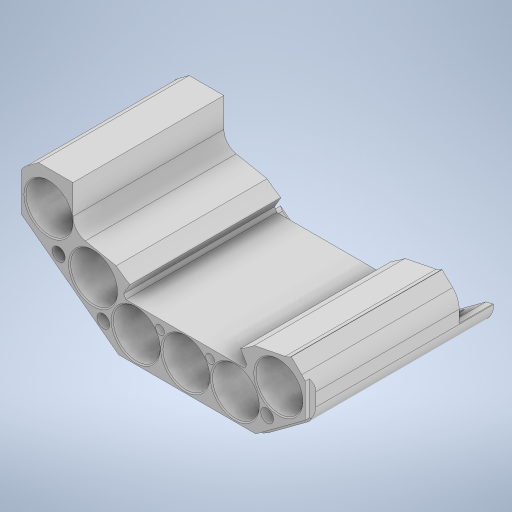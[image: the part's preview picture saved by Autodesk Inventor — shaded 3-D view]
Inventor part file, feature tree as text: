
AUTODESK INVENTOR PART (.ipt)
format: ipt  version: 2023.4 (Build 274418000, 418)  size: 566,272 bytes
history: native  units: mm
features: extrude x11, sketch x11, chamfer x3, projected_geometry x2, thicken_offset x1, fillet x1, mirror x1
ambient origin geometry x8: Origin, YZ Plane, XZ Plane, XY Plane, X Axis, Y Axis, Z Axis, Center Point
bodies: Solid1 (feature_tree)
feature tree (30):
  extrude  "Extrusion1"  Depth=70.0mm
  thicken_offset  "Thicken1"
  extrude  "Extrusion2"  Depth=21.7mm
  extrude  "Extrusion3"  Depth=21.7mm
  chamfer  "Chamfer1"  Distance=0.1mm
  extrude  "Extrusion4"  Depth=54.889727mm
  chamfer  "Chamfer2"  Distance=51.0mm
  extrude  "Extrusion6"  Depth=2.0mm
  extrude  "Extrusion7"  Depth=2.0mm
  extrude  "Extrusion8"  Depth=2.0mm
  extrude  "Extrusion9"  Depth=2.0mm
  extrude  "Extrusion10"  TaperAngle=0.0deg  [1 undecoded]
  extrude  "Extrusion11"  Depth=2.0mm
  fillet  "Fillet1"  Radius=102.0mm
  chamfer  "Chamfer5"  Distance=51.0mm
  mirror  "Mirror1"
  extrude  "Extrusion13"  Depth=1.5mm
  sketch  "Sketch1"  dims[d0=70.0mm d1=0.0mm d2=21.7mm]
  sketch  "Sketch2"  dims[d3=21.7mm d4=21.7mm]
  projected_geometry  "Projected Loop1"
  sketch  "Sketch3"  dims[d5=21.7mm d6=21.7mm]
  sketch  "Sketch4"  dims[d7=21.7mm d10=0.1mm d11=0.3mm]
  projected_geometry  "Projected Loop2"
  sketch  "Sketch6"  dims[d12=96.0mm d13=54.889727mm]
  sketch  "Sketch7"  dims[d14=54.889727mm]
  sketch  "Sketch8"  dims[d15=60.0mm]
  sketch  "Sketch9"  dims[d16=60.0mm]
  sketch  "Sketch10"  dims[d17=7.0mm]
  sketch  "Sketch11"  dims[d18=7.0mm]
  sketch  "Sketch16"  dims[d19=51.0mm d20=51.0mm d21=12.0mm d22=12.0mm d23=12.0mm d24=23.0mm d25=0.0mm d26=23.0mm d28=102.0mm d29=51.0mm d30=1.5mm d32=1.5mm d33=1.5mm d34=2.0mm d35=0.0mm d36=5.9mm d37=5.9mm d38=38.0mm d39=38.0mm d40=11.5mm d41=11.5mm d42=15.0mm d43=0.0mm d44=5.9mm d45=26.5mm d46=6.0mm d47=1.5mm d48=2.0mm d49=45.0deg d50=1.5mm d51=1.5mm d52=16.0mm d53=0.0mm d54=0.5mm d55=2.0mm d56=45.0deg d65=6.0mm d66=6.0mm d67=6.0mm d68=3.3mm d69=6.0mm d70=6.0mm d71=0.0mm d72=0.0mm d73=6.0mm d74=3.3mm d75=3.3mm d76=6.0mm d77=12.0mm d78=12.0mm d79=0.0mm d80=0.0mm d81=3.3mm d82=12.0mm d83=6.0mm d84=0.0mm d85=0.0mm d86=5.3mm d87=3.0mm d88=0.0mm d89=5.3mm d90=5.3mm d91=3.0mm d92=0.0mm d93=5.3mm d94=3.0mm d95=0.0mm d96=10.0mm d97=2.0mm d98=2.0mm d99=45.0deg d105=4.0mm d106=4.0mm d107=0.0mm d108=0.0mm]
note: 1 required parameter value undecoded (feature->parameter linkage not recoverable at this tier; creation-order binding heuristic only, values carry confidence <= 0.55)
